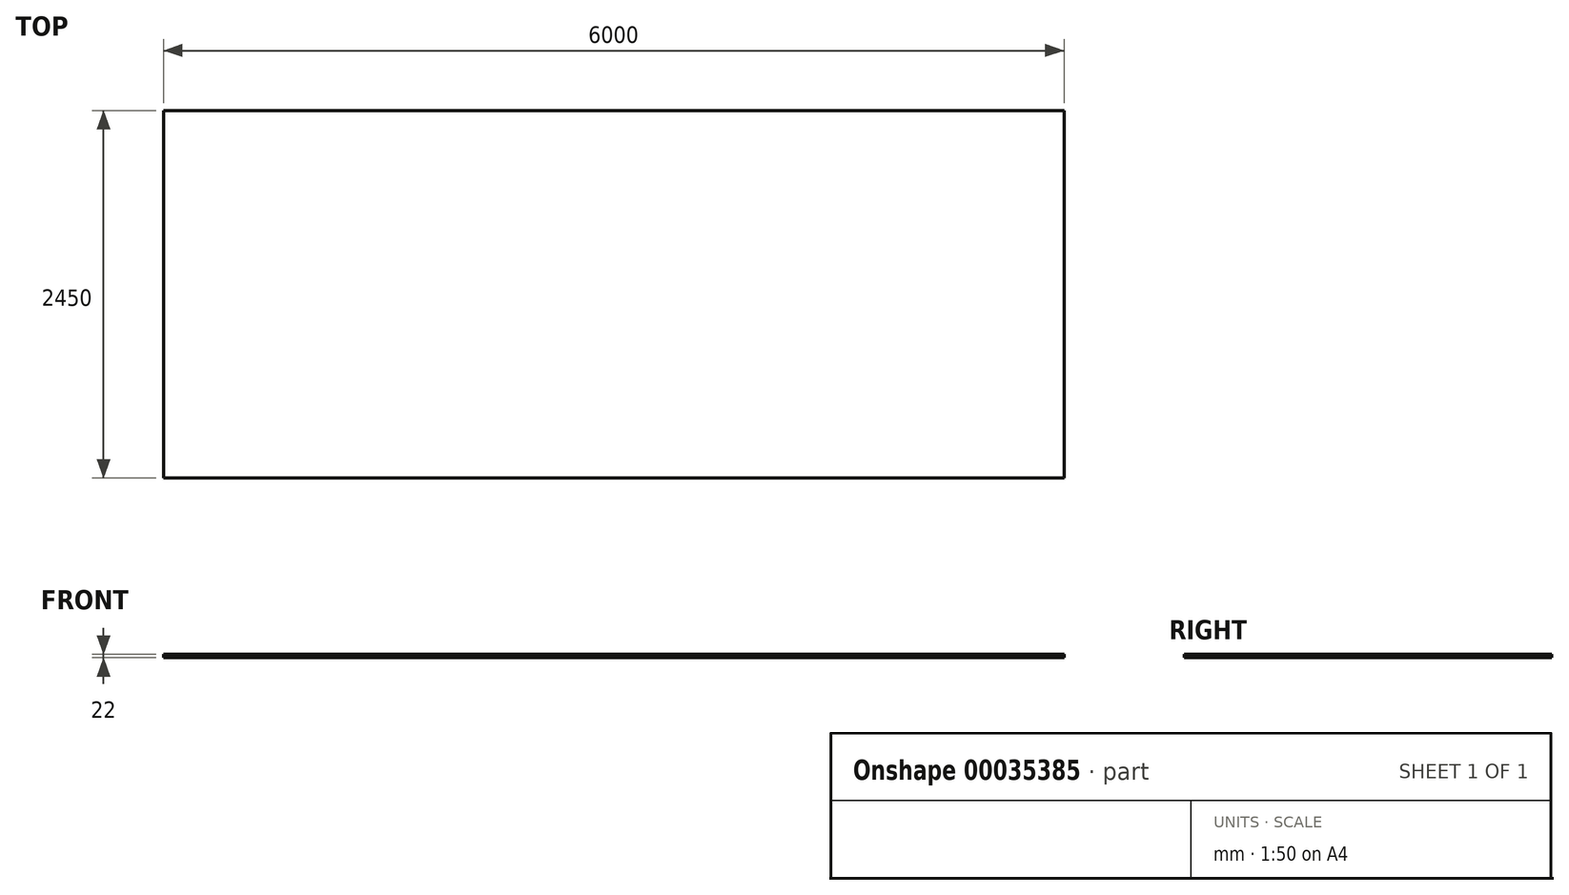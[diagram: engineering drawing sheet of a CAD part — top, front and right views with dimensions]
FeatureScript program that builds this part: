
annotation { "Feature Type Name" : "Feature", "Feature Type Description" : "" }
export const myFeature = defineFeature(function(context is Context, id is Id, definition is map)
    precondition{}
    {
        {
            var Q0;
            Q0=qCreatedBy(makeId("Top.planeOp"),FACE);
            var sketch = newSketch(context, id + "F0", { "sketchPlane" : qUnion([Q0])});
            skLineSegment(sketch, "E0.rect.bottom", {"start": v(3000, -1225) * mm, "end": v(-3000, -1225) * mm});
            skLineSegment(sketch, "E0.rect.top", {"start": v(3000, 1225) * mm, "end": v(-3000, 1225) * mm});
            skLineSegment(sketch, "E0.rect.left", {"start": v(3000, -1225) * mm, "end": v(3000, 1225) * mm});
            skLineSegment(sketch, "E0.rect.right", {"start": v(-3000, -1225) * mm, "end": v(-3000, 1225) * mm});
            skPoint(sketch, "E0.rect.middle", {"position": v(0, 0) * mm});
            skSolve(sketch);
        }
        {
            var Q0;
            Q0=makeQuery(id+"F0.imprint","IMPRINT",FACE,{"disambiguationData":[TD([[makeQuery(id+"F0.imprint","IMPRINT",EDGE,{"derivedFrom":sQuery(id+"F0.wireOp",EDGE,"E0.rect.bottom")}),-1.0]])]});
            extrude(context, id + "F1", {"entities" : qUnion([Q0]), "depth" : 22 * mm});
        }
    });
